# Revit family: 0048953
name_source: partatom
category: Lighting Fixtures
revit_build: Autodesk Revit 2017 (Build: 20190507_1515(x64)
units: mm (PartAtom-declared; Revit-internal decimal feet)

## family parameters
Cut with Voids When Loaded = No
Host = Face
Light Source = Yes
OmniClass Number = 23.80.70.00
OmniClass Title = Lighting
Part Type = Normal
Room Calculation Point = No
Round Connector Dimension = Use Diameter
Shared = No

## types (8) — shared parameters
Assembly Code = D5020200
AssetType = Fixed
ClassificationName = Uniclass2015
ClassificationValue = EF_70_80
Color Filter = 16777215
Default Elevation = 1219 mm
Dimming Lamp Color Temperature Shift = <None>
DocumentationLiterature = http://www.sylvania-lighting.com
ElectricShockClassification = Class I
Emit Shape Visible in Rendering = No
Emit from Circle Diameter = 610 mm  [stored 2.00131 ft]
GAP_SYL = 3 mm  [stored 0.00984252 ft]
HEIGHT_SYL = 77 mm
HOLE_HEIGHT_SYL = 24 mm
IfcExportAs = IfcLightFixtureType
IfcExportType = IfcLightFixtureType
ImpactProtectionIndex = IK08
IngressProtection = IP20
Keynote = 16500
LUM_R_SYL = 30 mm  [stored 0.0984252 ft]
Lamp = LED
LampColourRenderingIndex = 80
LampColourTemperature = 4000 K
LampMacAdamStep = 5
LampsType = LED
Manufacturer = Feilo Sylvania
ManufacturerName = Feilo Sylvania
Material = steel housing, pc polycarbonate diffuser
Material_1_SYL = Dynamo
Material_2_SYL = <By Category>
Material_3_SYL = <By Category>
Material_4_SYL = <By Category>
NominalDepth = 70 mm
NominalHeight = 77 mm
NominalLength = 1220 mm
PowerFactor = 0.9
R_HEIGHT_SYL = 44 mm
Tilt Angle = -90.00°
Type Image = <None>
URL = http://www.sylvania-lighting.com
Voltage = 0 V
WIDTH/2_SYL = 35 mm  [stored 0.114829 ft]
zero-valued in all types: Cost

## per-type parameters (varying)
| type | Apparent Load | Description | LampNominalLuminous | LuminousEfficacy | Model | ModelNumber | ModelReference | Name | Photometric Web File | PowerConsumption | TypeName | Weight |
| 0048940 WAYLINE 1200 MWCOR 3100LM 840 | 24 VA | LED batten, T8 replacement, ease of installation through 2 part push-in design of the housing (safety cable included), through wiring capability, steel housing, 3100lm, 24W, 129lm/W, 4000K, CRI80, 3 step MacAdam ellipse, symmetric wide beam angle, Class I, 90000 hrs L80B20 lifespan, non-dimmable driver, corridor function with microwave presence sensor, IK08, IP20, 1220 x 70 x 76.5mm  (L x W x H) dimensions, 1.73kg. | 3100 lm | 129 lm/W | Wayline 1200 MWCOR 3100lm 840 | 48940 | Wayline 1200 MWCOR 3100lm 840 | Wayline 1200 MWCOR 3100lm 840 | 0048940.ies | 24 W | Wayline 1200 MWCOR 3100lm 840 | 10.38 kg |
| 0048933 WAYLINE 1200 MW 5700LM 840 | 41 VA | LED batten, T8 replacement, ease of installation through 2 part push-in design of the housing (safety cable included), through wiring capability, steel housing, 5700lm, 41W, 139lm/W, 4000K, CRI80, 3 step MacAdam ellipse, symmetric wide beam angle, Class I, 90000 hrs L80B20 lifespan, non-dimmable driver, MW sensor for 360° detection up to 8m range at 6m mounting height, IK08, IP20, 1220 x 70 x 76.5mm (LxWxD) dimensions, 1.47kg weight. | 5700 lm | 139 lm/W | Wayline 1200 MW 5700lm 840 | 48933 | Wayline 1200 MW 5700lm 840 | Wayline 1200 MW 5700lm 840 | 0048933.ies | 41 W | Wayline 1200 MW 5700lm 840 | 8.82 kg |
| 0048932 WAYLINE 1200 MW 3200LM 840 | 24 VA | LED batten, T8 replacement, ease of installation through 2 part push-in design of the housing (safety cable included), through wiring capability, steel housing, 3200lm, 24W, 133lm/W, 4000K, CRI80, 3 step MacAdam ellipse, symmetric wide beam angle, Class I, 90000 hrs L80B20 lifespan, non-dimmable driver, MW sensor for 360° detection up to 8m range at 6m mounting height, IK08, IP20, 1220 x 70 x 76.5mm (LxWxD) dimensions, 1.44kg weight. | 3200 lm | 133 lm/W | Wayline 1200 MW 3200lm 840 | 48932 | Wayline 1200 MW 3200lm 840 | Wayline 1200 MW 3200lm 840 | 0048932.ies | 24 W | Wayline 1200 MW 3200lm 840 | 8.64 kg |
| 0048929 WAYLINE 1200 5700LM 840 EM | 44 VA | LED batten, T8 replacement, ease of installation through 2 part push-in design of the housing (safety cable included), through wiring capability, steel housing, 5700lm, 44W, 130lm/W, 4000K, CRI80, 3 step MacAdam ellipse, symmetric wide beam angle, Class I, 90000 hrs L80B20 lifespan, non-dimmable driver, 3-hour maintained emergency batteries, IK08, IP20, 1220 x  70 x 76.5mm  (L x W x H) dimensions, 1.82kg. | 5700 lm | 130 lm/W | Wayline 1200 5700lm 840 EM | 48929 | Wayline 1200 5700lm 840 EM | Wayline 1200 5700lm 840 EM | 0048929.ies | 44 W | Wayline 1200 5700lm 840 EM | 10.92 kg |
| 0048928 WAYLINE 1200 3200LM 840 EM | 26 VA | LED batten, T8 replacement, ease of installation through 2 part push-in design of the housing (safety cable included), through wiring capability, steel housing, 3200lm, 26W, 123lm/W, 4000K, CRI80, 3 step MacAdam ellipse, symmetric wide beam angle, Class I, 90000 hrs L80B20 lifespan, non-dimmable driver, 3-hour maintained emergency batteries, IK08, IP20, 1220 x 70 x 76.5mm  (L x W x H) dimensions, 1.78kg. | 3200 lm | 123 lm/W | Wayline 1200 3200lm 840 EM | 48928 | Wayline 1200 3200lm 840 EM | Wayline 1200 3200lm 840 EM | 0048928.ies | 26 W | Wayline 1200 3200lm 840 EM | 10.68 kg |
| 0048925 WAYLINE 1200 DALI 5500LM 840 | 40 VA | LED batten, T8 replacement, ease of installation through 2 part push-in design of the housing (safety cable included), through wiring capability, steel housing, 5500lm, 40W, 138lm/W, 4000K, CRI80, 3 step MacAdam ellipse, symmetric wide beam angle, Class I, 90000 hrs L80B20 lifespan, DALI dimmable driver, IK08, IP20, 1220 x 70 x 76.5mm (LxWxD) dimensions, 1.67kg weight. | 5500 lm | 138 lm/W | Wayline 1200 DALI 5500lm 840 | 48925 | Wayline 1200 DALI 5500lm 840 | Wayline 1200 DALI 5500lm 840 | 0048925.ies | 40 W | Wayline 1200 DALI 5500lm 840 | 10.02 kg |
| 0048924 WAYLINE 1200 DALI 3100LM 840 | 23 VA | LED batten, T8 replacement, ease of installation through 2 part push-in design of the housing (safety cable included), through wiring capability, steel housing, 3100lm, 23W, 135lm/W, 4000K, CRI80, 3 step MacAdam ellipse, symmetric wide beam angle, Class I, 90000 hrs L80B20 lifespan, DALI dimmable driver, IK08, IP20, 1220 x 70 x 76.5mm (LxWxD) dimensions, 1.66kg weight. | 3100 lm | 135 lm/W | Wayline 1200 DALI 3100lm 840 | 48924 | Wayline 1200 DALI 3100lm 840 | Wayline 1200 DALI 3100lm 840 | 0048924.ies | 23 W | Wayline 1200 DALI 3100lm 840 | 9.96 kg |
| 0048953 WAYLINE 1200 MWCOR 5500LM 840 | 41 VA | LED batten, T8 replacement, ease of installation through 2 part push-in design of the housing (safety cable included), through wiring capability, steel housing, 5500lm, 41W, 134lm/W, 4000K, CRI80, 3 step MacAdam ellipse, symmetric wide beam angle, Class I, 90000 hrs L80B20 lifespan, non-dimmable driver, corridor function with microwave presence sensor, IK08, IP20, 1220 x 70 x 76.5mm  (L x W x H) dimensions, 1.74kg. | 5500 lm | 134 lm/W | Wayline 1200 MWCOR 5500lm 840 | 48953 | Wayline 1200 MWCOR 5500lm 840 | Wayline 1200 MWCOR 5500lm 840 | 0048953.ies | 41 W | Wayline 1200 MWCOR 5500lm 840 | 10.44 kg |

note: [stored X ft] marks values corroborated as IEEE doubles in the binary element streams (Revit-internal decimal feet)

## geometry (parser evidence)
native form markers: Sweep x3
no freeform markers — native parametric forms only
